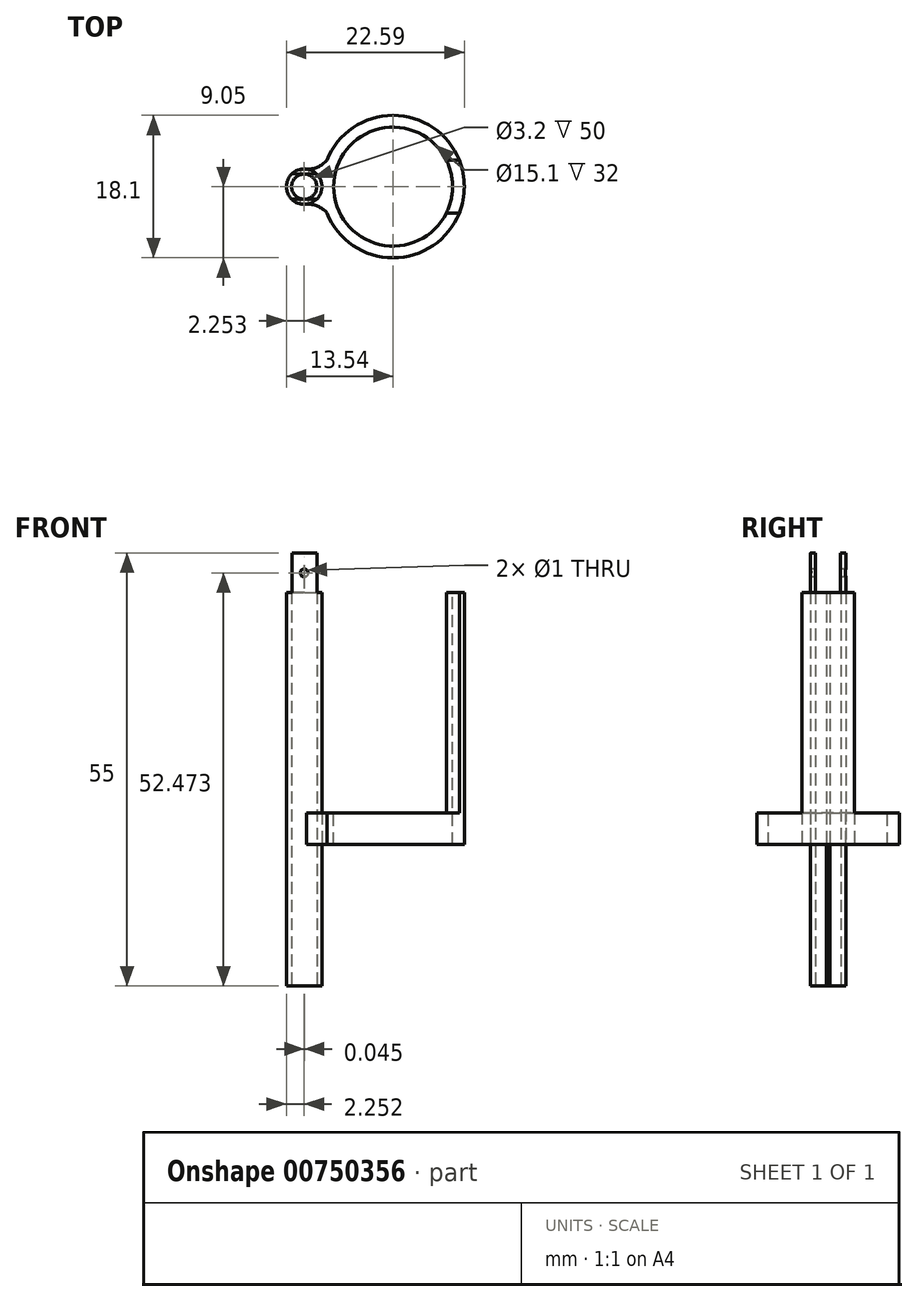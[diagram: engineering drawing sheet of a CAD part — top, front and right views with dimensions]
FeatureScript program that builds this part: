
annotation { "Feature Type Name" : "Feature", "Feature Type Description" : "" }
export const myFeature = defineFeature(function(context is Context, id is Id, definition is map)
    precondition{}
    {
        {
            var Q0;
            Q0=qCreatedBy(makeId("Top.planeOp"),FACE);
            var sketch = newSketch(context, id + "F0", { "sketchPlane" : qUnion([Q0])});
            skArc(sketch, "E0", {"start": v(-8.4, -3.34) * mm, "mid": v(9.05, 0) * mm, "end": v(-8.4, 3.34) * mm});
            skCircle(sketch, "E1", {"center": v(-11.29, 0) * mm, "radius": 1.6 * mm});
            skCircle(sketch, "E2", {"center": v(-11.29, 0) * mm, "radius": 2.25 * mm});
            skArc(sketch, "E3", {"start": v(-8.4, -3.34) * mm, "mid": v(-9.58, -2.48) * mm, "end": v(-11, -2.23) * mm});
            skArc(sketch, "E4.MirrorCS", {"start": v(-8.4, 3.34) * mm, "mid": v(-9.58, 2.48) * mm, "end": v(-11, 2.23) * mm});
            skArc(sketch, "E5.trimOffspring", {"start": v(-9.05, 0.22) * mm, "mid": v(-9.05, 0) * mm, "end": v(-9.05, -0.22) * mm});
            skSolve(sketch);
        }
        {
            var Q0;
            Q0=makeQuery(id+"F0.imprint","IMPRINT",FACE,{"disambiguationData":[TD([[makeQuery(id+"F0.imprint","IMPRINT",EDGE,{"derivedFrom":sQuery(id+"F0.wireOp",EDGE,"E1")}),-1.0]])]});
            extrude(context, id + "F1", {"entities" : qUnion([Q0]), "depth" : 25 * mm, "offsetDistance" : 25 * mm});
        }
        {
            var Q0;
            Q0=makeQuery(id+"F0.imprint","IMPRINT",FACE,{"disambiguationData":[TD([[makeQuery(id+"F0.imprint","IMPRINT",EDGE,{"derivedFrom":sQuery(id+"F0.wireOp",EDGE,"E1")}),-1.0]])]});
            extrude(context, id + "F2", {"entities" : qUnion([Q0]), "operationType" : NewBodyOperationType.ADD, "oppositeDirection" : true, "depth" : 20 * mm, "offsetDistance" : 25 * mm});
        }
        {
            var Q0;
            Q0=makeQuery(id+"F0.imprint","IMPRINT",FACE,{"disambiguationData":[TD([[makeQuery(id+"F0.imprint","IMPRINT",EDGE,{"derivedFrom":sQuery(id+"F0.wireOp",EDGE,"E0")}),1.0]])]});
            extrude(context, id + "F3", {"entities" : qUnion([Q0]), "operationType" : NewBodyOperationType.ADD, "endBound" : BoundingType.SYMMETRIC, "depth" : 4 * mm, "offsetDistance" : 25 * mm});
        }
        {
            var Q0;
            Q0=makeQuery(id+"F3.opExtrude","CAP_FACE",FACE,{"disambiguationData":[OSD([sQuery(id+"F0.wireOp",EDGE,"E0"),sQuery(id+"F0.wireOp",EDGE,"E2"),sQuery(id+"F0.wireOp",EDGE,"E3"),sQuery(id+"F0.wireOp",EDGE,"E4.MirrorCS")])],"isStart":false});
            var sketch = newSketch(context, id + "F4", { "sketchPlane" : qUnion([Q0])});
            skCircle(sketch, "E6", {"center": v(0, 0) * mm, "radius": 7.55 * mm});
            skSolve(sketch);
        }
        {
            var Q0;
            Q0=makeQuery(id+"F4.imprint","IMPRINT",FACE,{"disambiguationData":[TD([[makeQuery(id+"F4.imprint","IMPRINT",EDGE,{"derivedFrom":sQuery(id+"F4.wireOp",EDGE,"E6")}),1.0]])]});
            extrude(context, id + "F5", {"entities" : qUnion([Q0]), "operationType" : NewBodyOperationType.REMOVE, "oppositeDirection" : true, "depth" : 25 * mm, "offsetDistance" : 25 * mm});
        }
        {
            var Q0;
            Q0=makeQuery(id+"F1.opExtrude","CAP_FACE",FACE,{"disambiguationData":[OSD([sQuery(id+"F0.wireOp",EDGE,"E1"),sQuery(id+"F0.wireOp",EDGE,"E2"),sQuery(id+"F0.wireOp",EDGE,"E5.trimOffspring")])],"isStart":false});
            var sketch = newSketch(context, id + "F6", { "sketchPlane" : qUnion([Q0])});
            skLineSegment(sketch, "E7", {"start": v(-11.27, 1.6) * mm, "end": v(-9.69, 1.58) * mm});
            skLineSegment(sketch, "E8", {"start": v(-11.27, 1.6) * mm, "end": v(-12.85, 1.62) * mm});
            skLineSegment(sketch, "E9", {"start": v(-12.85, 1.62) * mm, "end": v(-12.85, 3.12) * mm});
            skLineSegment(sketch, "E10", {"start": v(-12.85, 3.12) * mm, "end": v(-9.69, 3.12) * mm});
            skLineSegment(sketch, "E11", {"start": v(-9.69, 1.58) * mm, "end": v(-9.69, 3.12) * mm});
            skLineSegment(sketch, "E12.MirrorCS", {"start": v(-12.85, -1.62) * mm, "end": v(-12.85, -3.12) * mm});
            skLineSegment(sketch, "E13.MirrorCS", {"start": v(-11.27, -1.6) * mm, "end": v(-12.85, -1.62) * mm});
            skLineSegment(sketch, "E14.MirrorCS", {"start": v(-11.27, -1.6) * mm, "end": v(-9.69, -1.58) * mm});
            skLineSegment(sketch, "E15.MirrorCS", {"start": v(-9.69, -1.58) * mm, "end": v(-9.69, -3.12) * mm});
            skLineSegment(sketch, "E16.MirrorCS", {"start": v(-12.85, -3.12) * mm, "end": v(-9.69, -3.12) * mm});
            skSolve(sketch);
        }
        {
            var Q0;
            {var subQ0=sQuery(id+"F6.wireOp",EDGE,"E7");Q0=makeQuery(id+"F6.imprint","IMPRINT",FACE,{"disambiguationData":[TD([[makeQuery(id+"F6.imprint","IMPRINT",EDGE,{"derivedFrom":subQ0}),1.0]])]});}
            var Q1;
            {var subQ0=sQuery(id+"F6.wireOp",EDGE,"E13.MirrorCS");Q1=makeQuery(id+"F6.imprint","IMPRINT",FACE,{"disambiguationData":[TD([[makeQuery(id+"F6.imprint","IMPRINT",EDGE,{"derivedFrom":subQ0}),1.0]])]});}
            extrude(context, id + "F7", {"entities" : qUnion([Q0, Q1]), "operationType" : NewBodyOperationType.ADD, "depth" : 10 * mm, "offsetDistance" : 25 * mm});
        }
        {
            var Q0;
            {var subQ0=sQuery(id+"F0.wireOp",EDGE,"E1");var subQ1=sQuery(id+"F0.wireOp",EDGE,"E2");var subQ2=sQuery(id+"F6.wireOp",EDGE,"E14.MirrorCS");var subQ3=sQuery(id+"F6.wireOp",EDGE,"E13.MirrorCS");var subQ4=makeQuery(id+"F1.opExtrude","CAP_FACE",FACE,{"disambiguationData":[OSD([subQ0,subQ1,sQuery(id+"F0.wireOp",EDGE,"E5.trimOffspring")])],"isStart":false});var subQ5=sQuery(id+"F6.wireOp",EDGE,"E8");var subQ6=sQuery(id+"F6.wireOp",EDGE,"E7");var subQ7=makeQuery(id+"F1.opExtrude","CAP_EDGE",EDGE,{"disambiguationData":[OSD([subQ1])],"isStart":false});Q0=makeQuery(id+"F7.boolean.opBoolean","SPLIT",FACE,{"disambiguationData":[TD([makeQuery(id+"F1.opExtrude","SWEPT_FACE",FACE,{"disambiguationData":[OSD([subQ0])]}),subQ4,makeQuery(id+"F1.opExtrude","SWEPT_FACE",FACE,{"disambiguationData":[OSD([subQ1])]}),makeQuery(id+"F2.opExtrude","SWEPT_FACE",FACE,{"disambiguationData":[OSD([subQ0])]}),makeQuery(id+"F2.opExtrude","SWEPT_FACE",FACE,{"disambiguationData":[OSD([subQ1])]}),makeQuery(id+"F7.opExtrude","SWEPT_FACE",FACE,{"disambiguationData":[OSD([subQ6,subQ5])]}),makeQuery(id+"F7.opExtrude","SWEPT_FACE",FACE,{"disambiguationData":[OSD([subQ3,subQ2])]}),makeQuery(id+"F7.opExtrude","SWEPT_FACE",FACE,{"disambiguationData":[OSD([subQ1]),TDD([makeQuery(id+"F6.imprint","IMPRINT",EDGE,{"disambiguationData":[TD([[makeQuery(id+"F6.imprint","INTERSECT",VERTEX,{"derivedFrom":[subQ7,subQ6,sQuery(id+"F6.wireOp",EDGE,"E11")]}),-1.0]])],"derivedFrom":subQ7})])]}),makeQuery(id+"F7.opExtrude","SWEPT_FACE",FACE,{"disambiguationData":[OSD([subQ1]),TDD([makeQuery(id+"F6.imprint","IMPRINT",EDGE,{"disambiguationData":[TD([[makeQuery(id+"F6.imprint","INTERSECT",VERTEX,{"derivedFrom":[subQ7,sQuery(id+"F6.wireOp",EDGE,"E12.MirrorCS"),subQ3]}),-1.0]])],"derivedFrom":subQ7})])]})])],"derivedFrom":subQ4});}
            var Q1;
            {var subQ0=sQuery(id+"F6.wireOp",EDGE,"E7");var subQ1=sQuery(id+"F0.wireOp",EDGE,"E2");var subQ2=makeQuery(id+"F1.opExtrude","CAP_EDGE",EDGE,{"disambiguationData":[OSD([subQ1])],"isStart":false});var subQ3=sQuery(id+"F6.wireOp",EDGE,"E8");var subQ4=sQuery(id+"F0.wireOp",EDGE,"E5.trimOffspring");var subQ5=sQuery(id+"F0.wireOp",EDGE,"E1");var subQ6=makeQuery(id+"F1.opExtrude","CAP_FACE",FACE,{"disambiguationData":[OSD([subQ5,subQ1,subQ4])],"isStart":false});var subQ7=sQuery(id+"F6.wireOp",EDGE,"E14.MirrorCS");var subQ8=sQuery(id+"F6.wireOp",EDGE,"E13.MirrorCS");Q1=makeQuery(id+"F7.boolean.opBoolean","SPLIT",FACE,{"disambiguationData":[TD([makeQuery(id+"F1.opExtrude","SWEPT_FACE",FACE,{"disambiguationData":[OSD([subQ5])]}),subQ6,makeQuery(id+"F1.opExtrude","SWEPT_FACE",FACE,{"disambiguationData":[OSD([subQ1])]}),makeQuery(id+"F1.opExtrude","SWEPT_FACE",FACE,{"disambiguationData":[OSD([subQ4])]}),makeQuery(id+"F2.opExtrude","SWEPT_FACE",FACE,{"disambiguationData":[OSD([subQ5])]}),makeQuery(id+"F2.opExtrude","SWEPT_FACE",FACE,{"disambiguationData":[OSD([subQ1])]}),makeQuery(id+"F2.opExtrude","SWEPT_FACE",FACE,{"disambiguationData":[OSD([subQ4])]}),makeQuery(id+"F7.opExtrude","SWEPT_FACE",FACE,{"disambiguationData":[OSD([subQ0,subQ3])]}),makeQuery(id+"F7.opExtrude","SWEPT_FACE",FACE,{"disambiguationData":[OSD([subQ8,subQ7])]}),makeQuery(id+"F7.opExtrude","SWEPT_FACE",FACE,{"disambiguationData":[OSD([subQ1]),TDD([makeQuery(id+"F6.imprint","IMPRINT",EDGE,{"disambiguationData":[TD([[makeQuery(id+"F6.imprint","INTERSECT",VERTEX,{"derivedFrom":[subQ2,subQ0,sQuery(id+"F6.wireOp",EDGE,"E11")]}),-1.0]])],"derivedFrom":subQ2})])]}),makeQuery(id+"F7.opExtrude","SWEPT_FACE",FACE,{"disambiguationData":[OSD([subQ1]),TDD([makeQuery(id+"F6.imprint","IMPRINT",EDGE,{"disambiguationData":[TD([[makeQuery(id+"F6.imprint","INTERSECT",VERTEX,{"derivedFrom":[subQ2,sQuery(id+"F6.wireOp",EDGE,"E12.MirrorCS"),subQ8]}),-1.0]])],"derivedFrom":subQ2})])]})])],"derivedFrom":subQ6});}
            extrude(context, id + "F8", {"entities" : qUnion([Q0, Q1]), "operationType" : NewBodyOperationType.ADD, "depth" : 5 * mm, "offsetDistance" : 25 * mm});
        }
        {
            var Q0;
            Q0=makeQuery(id+"F7.opExtrude","SWEPT_FACE",FACE,{"disambiguationData":[OSD([sQuery(id+"F6.wireOp",EDGE,"E7"),sQuery(id+"F6.wireOp",EDGE,"E8")])]});
            var sketch = newSketch(context, id + "F9", { "sketchPlane" : qUnion([Q0])});
            skCircle(sketch, "E17", {"center": v(-11.27, 32.47) * mm, "radius": 0.5 * mm});
            skSolve(sketch);
        }
        {
            var Q0;
            Q0=makeQuery(id+"F9.imprint","IMPRINT",FACE,{"disambiguationData":[TD([[makeQuery(id+"F9.imprint","IMPRINT",EDGE,{"derivedFrom":sQuery(id+"F9.wireOp",EDGE,"E17")}),1.0]])]});
            extrude(context, id + "F10", {"entities" : qUnion([Q0]), "operationType" : NewBodyOperationType.REMOVE, "endBound" : BoundingType.SYMMETRIC, "oppositeDirection" : true, "depth" : 25 * mm, "offsetDistance" : 25 * mm});
        }
        {
            var Q0;
            Q0=makeQuery(id+"F3.opExtrude","CAP_FACE",FACE,{"disambiguationData":[OSD([sQuery(id+"F0.wireOp",EDGE,"E0"),sQuery(id+"F0.wireOp",EDGE,"E2"),sQuery(id+"F0.wireOp",EDGE,"E3"),sQuery(id+"F0.wireOp",EDGE,"E4.MirrorCS")])],"isStart":false});
            var sketch = newSketch(context, id + "F11", { "sketchPlane" : qUnion([Q0])});
            skLineSegment(sketch, "E18", {"start": v(-8.4, -3.34) * mm, "end": v(8.4, -3.34) * mm});
            skLineSegment(sketch, "E19.MirrorCS", {"start": v(-8.4, 3.34) * mm, "end": v(8.4, 3.34) * mm});
            skSolve(sketch);
        }
        {
            var Q0;
            {var subQ0=sQuery(id+"F11.wireOp",EDGE,"E18");var subQ1=makeQuery(id+"F3.opExtrude","CAP_EDGE",EDGE,{"disambiguationData":[OSD([sQuery(id+"F0.wireOp",EDGE,"E0")])],"isStart":false});var subQ2=makeQuery(id+"F11.imprint","INTERSECT",VERTEX,{"derivedFrom":[subQ1,subQ0]});Q0=makeQuery(id+"F11.imprint","IMPRINT",FACE,{"disambiguationData":[TD([[makeQuery(id+"F11.imprint","IMPRINT",EDGE,{"disambiguationData":[TD([[subQ2,1.0]])],"derivedFrom":subQ0}),1.0]])]});}
            extrude(context, id + "F12", {"entities" : qUnion([Q0]), "operationType" : NewBodyOperationType.ADD, "depth" : 28 * mm, "offsetDistance" : 25 * mm});
        }
    });
